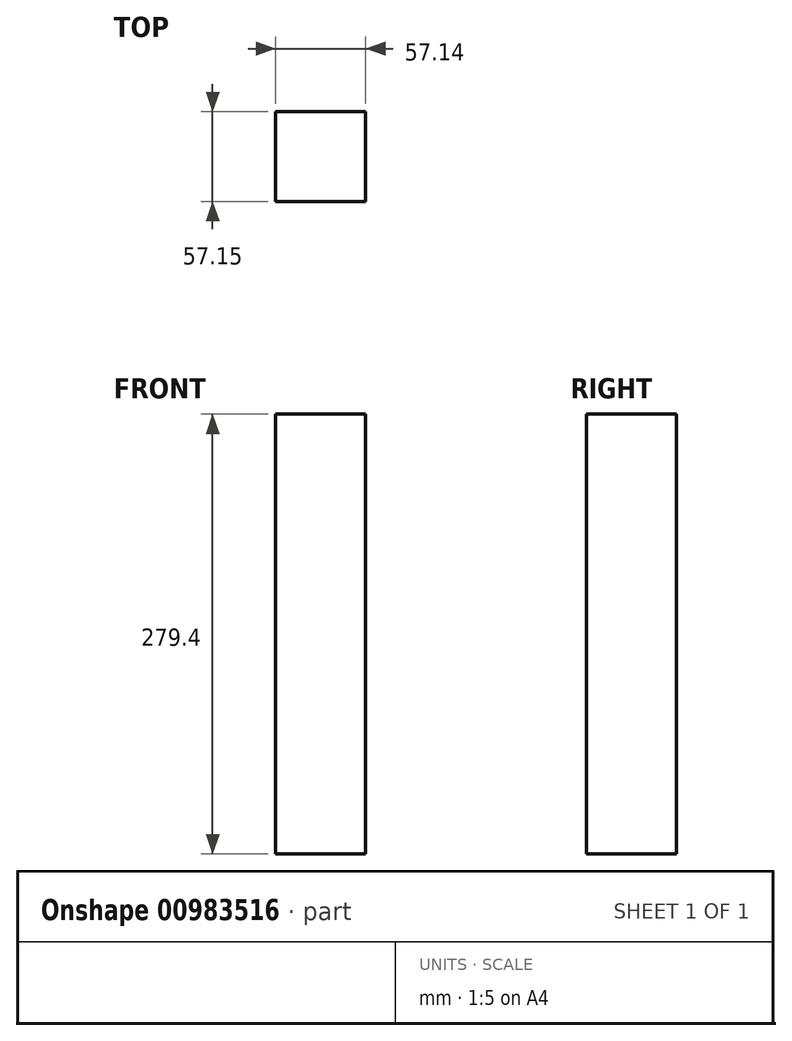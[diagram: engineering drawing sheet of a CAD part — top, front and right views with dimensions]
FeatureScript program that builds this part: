
annotation { "Feature Type Name" : "Feature", "Feature Type Description" : "" }
export const myFeature = defineFeature(function(context is Context, id is Id, definition is map)
    precondition{}
    {
        {
            var Q0;
            Q0=qCreatedBy(makeId("Top.planeOp"),FACE);
            var sketch = newSketch(context, id + "F0", { "sketchPlane" : qUnion([Q0])});
            skLineSegment(sketch, "E0.bottom", {"start": v(-28.58, 25.88) * mm, "end": v(28.58, 25.88) * mm});
            skLineSegment(sketch, "E0.top", {"start": v(-28.58, -31.27) * mm, "end": v(28.58, -31.27) * mm});
            skLineSegment(sketch, "E0.left", {"start": v(-28.58, 25.88) * mm, "end": v(-28.58, -31.27) * mm});
            skLineSegment(sketch, "E0.right", {"start": v(28.58, 25.88) * mm, "end": v(28.58, -31.27) * mm});
            skSolve(sketch);
        }
        {
            var Q0;
            Q0 = qSketchRegion(id + "F0", true);
            extrude(context, id + "F1", {"entities" : qUnion([Q0]), "depth" : 279.4 * mm, "offsetDistance" : 25.4 * mm});
        }
    });
